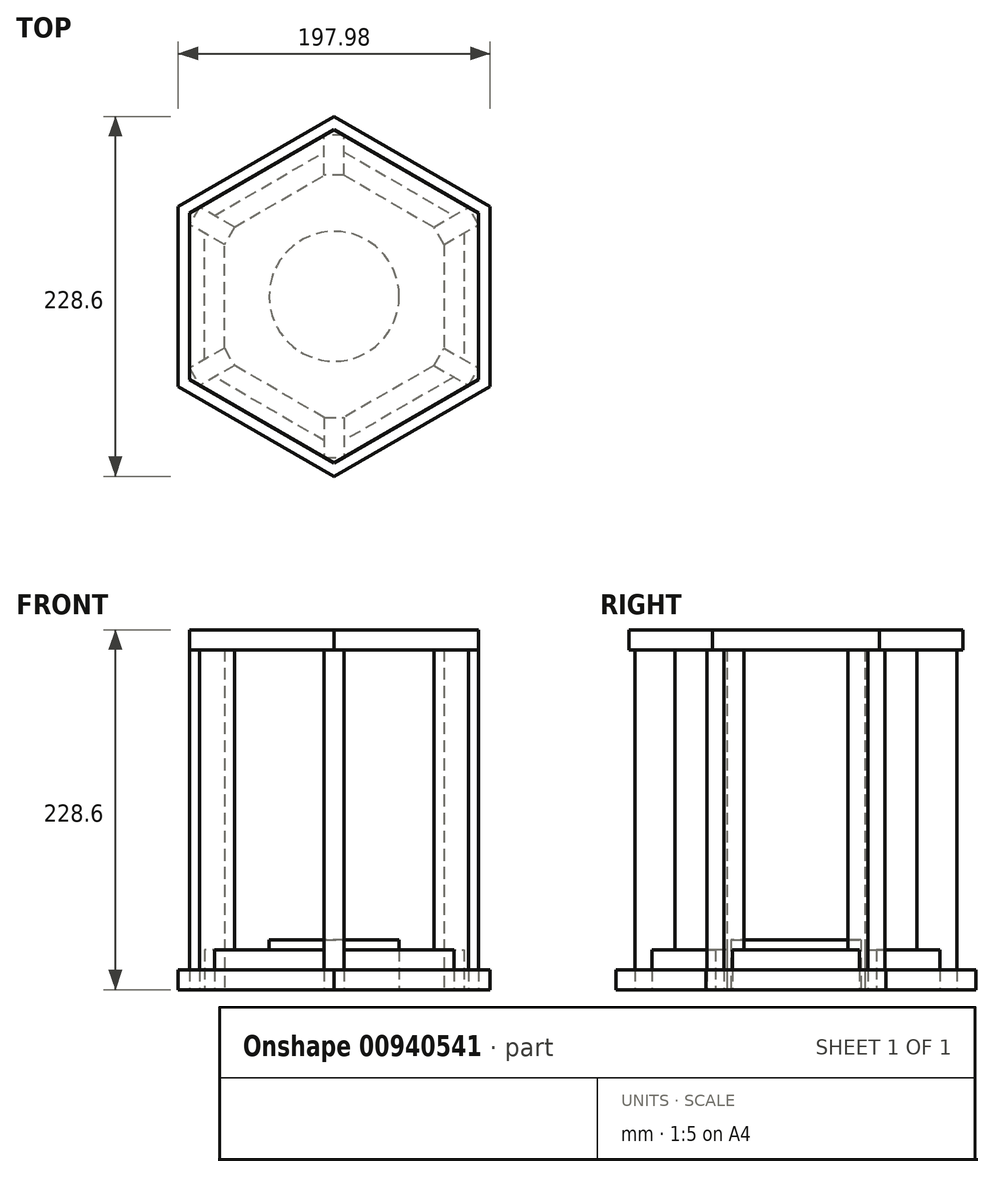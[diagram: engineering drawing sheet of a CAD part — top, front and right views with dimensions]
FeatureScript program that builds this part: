
annotation { "Feature Type Name" : "Feature", "Feature Type Description" : "" }
export const myFeature = defineFeature(function(context is Context, id is Id, definition is map)
    precondition{}
    {
        {
            var Q0;
            Q0=qCreatedBy(makeId("Top.planeOp"),FACE);
            var sketch = newSketch(context, id + "F0", { "sketchPlane" : qUnion([Q0])});
            skCircle(sketch, "E0.cCircle", {"center": v(0, 0) * mm, "radius": 82.45 * mm, "construction": true});
            skLineSegment(sketch, "E0.0", {"start": v(82.45, 47.6) * mm, "end": v(82.45, -47.6) * mm});
            skLineSegment(sketch, "E0.1", {"start": v(82.45, -47.6) * mm, "end": v(0, -95.2) * mm});
            skLineSegment(sketch, "E0.2", {"start": v(0, -95.2) * mm, "end": v(-82.45, -47.6) * mm});
            skLineSegment(sketch, "E0.3", {"start": v(-82.45, -47.6) * mm, "end": v(-82.45, 47.6) * mm});
            skLineSegment(sketch, "E0.4", {"start": v(-82.45, 47.6) * mm, "end": v(0, 95.2) * mm});
            skLineSegment(sketch, "E0.5", {"start": v(0, 95.2) * mm, "end": v(82.45, 47.6) * mm});
            skPoint(sketch, "E0.0.midPoint", {"position": v(82.45, 0) * mm});
            skCircle(sketch, "E1.cCircle", {"center": v(0, 0) * mm, "radius": 69.75 * mm, "construction": true});
            skLineSegment(sketch, "E1.0", {"start": v(69.75, 40.27) * mm, "end": v(69.75, -40.27) * mm});
            skLineSegment(sketch, "E1.1", {"start": v(69.75, -40.27) * mm, "end": v(0, -80.54) * mm});
            skLineSegment(sketch, "E1.2", {"start": v(0, -80.54) * mm, "end": v(-69.75, -40.27) * mm});
            skLineSegment(sketch, "E1.3", {"start": v(-69.75, -40.27) * mm, "end": v(-69.75, 40.27) * mm});
            skLineSegment(sketch, "E1.4", {"start": v(-69.75, 40.27) * mm, "end": v(0, 80.54) * mm});
            skLineSegment(sketch, "E1.5", {"start": v(0, 80.54) * mm, "end": v(69.75, 40.27) * mm});
            skPoint(sketch, "E1.0.midPoint", {"position": v(69.75, 0) * mm});
            skLineSegment(sketch, "E2.bottom", {"start": v(6.35, 76.88) * mm, "end": v(-6.35, 76.88) * mm});
            skLineSegment(sketch, "E2.top", {"start": v(6.35, 102.28) * mm, "end": v(-6.35, 102.28) * mm});
            skLineSegment(sketch, "E2.left", {"start": v(6.35, 76.88) * mm, "end": v(6.35, 102.28) * mm});
            skLineSegment(sketch, "E2.right", {"start": v(-6.35, 76.88) * mm, "end": v(-6.35, 102.28) * mm});
            skPoint(sketch, "E2.middle", {"position": v(0, 89.58) * mm});
            skLineSegment(sketch, "E3.1.0", {"start": v(-63.4, 43.94) * mm, "end": v(-69.75, 32.94) * mm});
            skLineSegment(sketch, "E3.1.1", {"start": v(-85.4, 56.64) * mm, "end": v(-91.75, 45.64) * mm});
            skLineSegment(sketch, "E3.1.2", {"start": v(-63.4, 43.94) * mm, "end": v(-85.4, 56.64) * mm});
            skLineSegment(sketch, "E3.1.3", {"start": v(-69.75, 32.94) * mm, "end": v(-91.75, 45.64) * mm});
            skLineSegment(sketch, "E3.2.0", {"start": v(-69.75, -32.94) * mm, "end": v(-63.4, -43.94) * mm});
            skLineSegment(sketch, "E3.2.1", {"start": v(-91.75, -45.64) * mm, "end": v(-85.4, -56.64) * mm});
            skLineSegment(sketch, "E3.2.2", {"start": v(-69.75, -32.94) * mm, "end": v(-91.75, -45.64) * mm});
            skLineSegment(sketch, "E3.2.3", {"start": v(-63.4, -43.94) * mm, "end": v(-85.4, -56.64) * mm});
            skLineSegment(sketch, "E3.3.0", {"start": v(-6.35, -76.88) * mm, "end": v(6.35, -76.88) * mm});
            skLineSegment(sketch, "E3.3.1", {"start": v(-6.35, -102.28) * mm, "end": v(6.35, -102.28) * mm});
            skLineSegment(sketch, "E3.3.2", {"start": v(-6.35, -76.88) * mm, "end": v(-6.35, -102.28) * mm});
            skLineSegment(sketch, "E3.3.3", {"start": v(6.35, -76.88) * mm, "end": v(6.35, -102.28) * mm});
            skLineSegment(sketch, "E3.4.0", {"start": v(63.4, -43.94) * mm, "end": v(69.75, -32.94) * mm});
            skLineSegment(sketch, "E3.4.1", {"start": v(85.4, -56.64) * mm, "end": v(91.75, -45.64) * mm});
            skLineSegment(sketch, "E3.4.2", {"start": v(63.4, -43.94) * mm, "end": v(85.4, -56.64) * mm});
            skLineSegment(sketch, "E3.4.3", {"start": v(69.75, -32.94) * mm, "end": v(91.75, -45.64) * mm});
            skLineSegment(sketch, "E3.5.0", {"start": v(69.75, 32.94) * mm, "end": v(63.4, 43.94) * mm});
            skLineSegment(sketch, "E3.5.1", {"start": v(91.75, 45.64) * mm, "end": v(85.4, 56.64) * mm});
            skLineSegment(sketch, "E3.5.2", {"start": v(69.75, 32.94) * mm, "end": v(91.75, 45.64) * mm});
            skLineSegment(sketch, "E3.5.3", {"start": v(63.4, 43.94) * mm, "end": v(85.4, 56.64) * mm});
            skCircle(sketch, "E4", {"center": v(0, 0) * mm, "radius": 41.28 * mm});
            skCircle(sketch, "E5.cCircle", {"center": v(0, 0) * mm, "radius": 98.99 * mm, "construction": true});
            skLineSegment(sketch, "E5.0", {"start": v(98.99, 57.15) * mm, "end": v(98.99, -57.15) * mm});
            skLineSegment(sketch, "E5.1", {"start": v(98.99, -57.15) * mm, "end": v(0, -114.3) * mm});
            skLineSegment(sketch, "E5.2", {"start": v(0, -114.3) * mm, "end": v(-98.99, -57.15) * mm});
            skLineSegment(sketch, "E5.3", {"start": v(-98.99, -57.15) * mm, "end": v(-98.99, 57.15) * mm});
            skLineSegment(sketch, "E5.4", {"start": v(-98.99, 57.15) * mm, "end": v(0, 114.3) * mm});
            skLineSegment(sketch, "E5.5", {"start": v(0, 114.3) * mm, "end": v(98.99, 57.15) * mm});
            skPoint(sketch, "E5.0.midPoint", {"position": v(98.99, 0) * mm});
            skSolve(sketch);
        }
        {
            var Q0;
            Q0=makeQuery(id+"F0.imprint","IMPRINT",FACE,{"disambiguationData":[TD([[makeQuery(id+"F0.imprint","IMPRINT",EDGE,{"derivedFrom":sQuery(id+"F0.wireOp",EDGE,"E4")}),1.0]])]});
            var Q1;
            {var subQ1=sQuery(id+"F0.wireOp",EDGE,"E3.5.1");Q1=makeQuery(id+"F0.imprint","IMPRINT",FACE,{"disambiguationData":[TD([[makeQuery(id+"F0.imprint","IMPRINT",EDGE,{"derivedFrom":subQ1}),1.0]])]});}
            var Q2;
            {var subQ0=sQuery(id+"F0.wireOp",EDGE,"E2.left");var subQ1=sQuery(id+"F0.wireOp",EDGE,"E0.5");var subQ2=makeQuery(id+"F0.imprint","INTERSECT",VERTEX,{"derivedFrom":[subQ1,subQ0]});Q2=makeQuery(id+"F0.imprint","IMPRINT",FACE,{"disambiguationData":[TD([[makeQuery(id+"F0.imprint","IMPRINT",EDGE,{"disambiguationData":[TD([[subQ2,-1.0]])],"derivedFrom":subQ1}),-1.0]])]});}
            var Q3;
            {var subQ6=sQuery(id+"F0.wireOp",EDGE,"E0.5");var subQ7=sQuery(id+"F0.wireOp",EDGE,"E0.0");var subQ8=makeQuery(id+"F0.imprint","INTERSECT",VERTEX,{"derivedFrom":[subQ7,subQ6]});Q3=makeQuery(id+"F0.imprint","IMPRINT",FACE,{"disambiguationData":[TD([[makeQuery(id+"F0.imprint","IMPRINT",EDGE,{"disambiguationData":[TD([[subQ8,-1.0]])],"derivedFrom":subQ7}),-1.0]])]});}
            var Q4;
            {var subQ1=sQuery(id+"F0.wireOp",EDGE,"E2.bottom");Q4=makeQuery(id+"F0.imprint","IMPRINT",FACE,{"disambiguationData":[TD([[makeQuery(id+"F0.imprint","IMPRINT",EDGE,{"derivedFrom":subQ1}),1.0]])]});}
            var Q5;
            {var subQ0=sQuery(id+"F0.wireOp",EDGE,"E3.4.2");var subQ1=sQuery(id+"F0.wireOp",EDGE,"E0.1");var subQ2=makeQuery(id+"F0.imprint","INTERSECT",VERTEX,{"derivedFrom":[subQ1,subQ0]});Q5=makeQuery(id+"F0.imprint","IMPRINT",FACE,{"disambiguationData":[TD([[makeQuery(id+"F0.imprint","IMPRINT",EDGE,{"disambiguationData":[TD([[subQ2,-1.0]])],"derivedFrom":subQ1}),-1.0]])]});}
            var Q6;
            {var subQ8=sQuery(id+"F0.wireOp",EDGE,"E0.2");var subQ10=sQuery(id+"F0.wireOp",EDGE,"E0.1");var subQ11=makeQuery(id+"F0.imprint","INTERSECT",VERTEX,{"derivedFrom":[subQ10,subQ8]});Q6=makeQuery(id+"F0.imprint","IMPRINT",FACE,{"disambiguationData":[TD([[makeQuery(id+"F0.imprint","IMPRINT",EDGE,{"disambiguationData":[TD([[subQ11,1.0]])],"derivedFrom":subQ10}),-1.0]])]});}
            var Q7;
            {var subQ8=sQuery(id+"F0.wireOp",EDGE,"E0.0");var subQ10=sQuery(id+"F0.wireOp",EDGE,"E0.1");var subQ11=makeQuery(id+"F0.imprint","INTERSECT",VERTEX,{"derivedFrom":[subQ8,subQ10]});Q7=makeQuery(id+"F0.imprint","IMPRINT",FACE,{"disambiguationData":[TD([[makeQuery(id+"F0.imprint","IMPRINT",EDGE,{"disambiguationData":[TD([[subQ11,1.0]])],"derivedFrom":subQ8}),-1.0]])]});}
            var Q8;
            {var subQ0=sQuery(id+"F0.wireOp",EDGE,"E3.4.1");Q8=makeQuery(id+"F0.imprint","IMPRINT",FACE,{"disambiguationData":[TD([[makeQuery(id+"F0.imprint","IMPRINT",EDGE,{"derivedFrom":subQ0}),1.0]])]});}
            var Q9;
            {var subQ31=sQuery(id+"F0.wireOp",EDGE,"E2.top");Q9=makeQuery(id+"F0.imprint","IMPRINT",FACE,{"disambiguationData":[TD([[makeQuery(id+"F0.imprint","IMPRINT",EDGE,{"derivedFrom":subQ31}),-1.0]])]});}
            var Q10;
            {var subQ0=sQuery(id+"F0.wireOp",EDGE,"E3.5.2");var subQ1=sQuery(id+"F0.wireOp",EDGE,"E0.0");var subQ2=makeQuery(id+"F0.imprint","INTERSECT",VERTEX,{"derivedFrom":[subQ1,subQ0]});Q10=makeQuery(id+"F0.imprint","IMPRINT",FACE,{"disambiguationData":[TD([[makeQuery(id+"F0.imprint","IMPRINT",EDGE,{"disambiguationData":[TD([[subQ2,-1.0]])],"derivedFrom":subQ1}),-1.0]])]});}
            var Q11;
            {var subQ1=sQuery(id+"F0.wireOp",EDGE,"E3.3.1");Q11=makeQuery(id+"F0.imprint","IMPRINT",FACE,{"disambiguationData":[TD([[makeQuery(id+"F0.imprint","IMPRINT",EDGE,{"derivedFrom":subQ1}),1.0]])]});}
            var Q12;
            {var subQ8=sQuery(id+"F0.wireOp",EDGE,"E0.5");var subQ9=sQuery(id+"F0.wireOp",EDGE,"E0.4");var subQ10=makeQuery(id+"F0.imprint","INTERSECT",VERTEX,{"derivedFrom":[subQ9,subQ8]});Q12=makeQuery(id+"F0.imprint","IMPRINT",FACE,{"disambiguationData":[TD([[makeQuery(id+"F0.imprint","IMPRINT",EDGE,{"disambiguationData":[TD([[subQ10,1.0]])],"derivedFrom":subQ9}),-1.0]])]});}
            var Q13;
            {var subQ0=sQuery(id+"F0.wireOp",EDGE,"E3.1.2");var subQ1=sQuery(id+"F0.wireOp",EDGE,"E0.4");var subQ2=makeQuery(id+"F0.imprint","INTERSECT",VERTEX,{"derivedFrom":[subQ1,subQ0]});Q13=makeQuery(id+"F0.imprint","IMPRINT",FACE,{"disambiguationData":[TD([[makeQuery(id+"F0.imprint","IMPRINT",EDGE,{"disambiguationData":[TD([[subQ2,-1.0]])],"derivedFrom":subQ1}),-1.0]])]});}
            var Q14;
            {var subQ0=sQuery(id+"F0.wireOp",EDGE,"E2.top");Q14=makeQuery(id+"F0.imprint","IMPRINT",FACE,{"disambiguationData":[TD([[makeQuery(id+"F0.imprint","IMPRINT",EDGE,{"derivedFrom":subQ0}),1.0]])]});}
            var Q15;
            {var subQ8=sQuery(id+"F0.wireOp",EDGE,"E0.4");var subQ9=sQuery(id+"F0.wireOp",EDGE,"E0.3");var subQ10=makeQuery(id+"F0.imprint","INTERSECT",VERTEX,{"derivedFrom":[subQ9,subQ8]});Q15=makeQuery(id+"F0.imprint","IMPRINT",FACE,{"disambiguationData":[TD([[makeQuery(id+"F0.imprint","IMPRINT",EDGE,{"disambiguationData":[TD([[subQ10,1.0]])],"derivedFrom":subQ9}),-1.0]])]});}
            var Q16;
            {var subQ0=sQuery(id+"F0.wireOp",EDGE,"E3.2.2");var subQ1=sQuery(id+"F0.wireOp",EDGE,"E0.3");var subQ2=makeQuery(id+"F0.imprint","INTERSECT",VERTEX,{"derivedFrom":[subQ1,subQ0]});Q16=makeQuery(id+"F0.imprint","IMPRINT",FACE,{"disambiguationData":[TD([[makeQuery(id+"F0.imprint","IMPRINT",EDGE,{"disambiguationData":[TD([[subQ2,-1.0]])],"derivedFrom":subQ1}),-1.0]])]});}
            var Q17;
            {var subQ1=sQuery(id+"F0.wireOp",EDGE,"E3.1.1");Q17=makeQuery(id+"F0.imprint","IMPRINT",FACE,{"disambiguationData":[TD([[makeQuery(id+"F0.imprint","IMPRINT",EDGE,{"derivedFrom":subQ1}),1.0]])]});}
            var Q18;
            {var subQ8=sQuery(id+"F0.wireOp",EDGE,"E0.3");var subQ9=sQuery(id+"F0.wireOp",EDGE,"E0.2");var subQ10=makeQuery(id+"F0.imprint","INTERSECT",VERTEX,{"derivedFrom":[subQ9,subQ8]});Q18=makeQuery(id+"F0.imprint","IMPRINT",FACE,{"disambiguationData":[TD([[makeQuery(id+"F0.imprint","IMPRINT",EDGE,{"disambiguationData":[TD([[subQ10,1.0]])],"derivedFrom":subQ9}),-1.0]])]});}
            var Q19;
            {var subQ0=sQuery(id+"F0.wireOp",EDGE,"E3.3.2");var subQ1=sQuery(id+"F0.wireOp",EDGE,"E0.2");var subQ2=makeQuery(id+"F0.imprint","INTERSECT",VERTEX,{"derivedFrom":[subQ1,subQ0]});Q19=makeQuery(id+"F0.imprint","IMPRINT",FACE,{"disambiguationData":[TD([[makeQuery(id+"F0.imprint","IMPRINT",EDGE,{"disambiguationData":[TD([[subQ2,-1.0]])],"derivedFrom":subQ1}),-1.0]])]});}
            var Q20;
            {var subQ1=sQuery(id+"F0.wireOp",EDGE,"E3.2.1");Q20=makeQuery(id+"F0.imprint","IMPRINT",FACE,{"disambiguationData":[TD([[makeQuery(id+"F0.imprint","IMPRINT",EDGE,{"derivedFrom":subQ1}),1.0]])]});}
            var Q21;
            {var subQ3=sQuery(id+"F0.wireOp",EDGE,"E3.3.0");Q21=makeQuery(id+"F0.imprint","IMPRINT",FACE,{"disambiguationData":[TD([[makeQuery(id+"F0.imprint","IMPRINT",EDGE,{"derivedFrom":subQ3}),-1.0]])]});}
            var Q22;
            {var subQ3=sQuery(id+"F0.wireOp",EDGE,"E2.bottom");Q22=makeQuery(id+"F0.imprint","IMPRINT",FACE,{"disambiguationData":[TD([[makeQuery(id+"F0.imprint","IMPRINT",EDGE,{"derivedFrom":subQ3}),-1.0]])]});}
            var Q23;
            {var subQ3=sQuery(id+"F0.wireOp",EDGE,"E3.4.0");Q23=makeQuery(id+"F0.imprint","IMPRINT",FACE,{"disambiguationData":[TD([[makeQuery(id+"F0.imprint","IMPRINT",EDGE,{"derivedFrom":subQ3}),-1.0]])]});}
            var Q24;
            {var subQ3=sQuery(id+"F0.wireOp",EDGE,"E3.1.0");Q24=makeQuery(id+"F0.imprint","IMPRINT",FACE,{"disambiguationData":[TD([[makeQuery(id+"F0.imprint","IMPRINT",EDGE,{"derivedFrom":subQ3}),-1.0]])]});}
            var Q25;
            {var subQ3=sQuery(id+"F0.wireOp",EDGE,"E3.2.0");Q25=makeQuery(id+"F0.imprint","IMPRINT",FACE,{"disambiguationData":[TD([[makeQuery(id+"F0.imprint","IMPRINT",EDGE,{"derivedFrom":subQ3}),-1.0]])]});}
            var Q26;
            {var subQ3=sQuery(id+"F0.wireOp",EDGE,"E3.5.0");Q26=makeQuery(id+"F0.imprint","IMPRINT",FACE,{"disambiguationData":[TD([[makeQuery(id+"F0.imprint","IMPRINT",EDGE,{"derivedFrom":subQ3}),-1.0]])]});}
            extrude(context, id + "F1", {"entities" : qUnion([Q0, Q1, Q2, Q3, Q4, Q5, Q6, Q7, Q8, Q9, Q10, Q11, Q12, Q13, Q14, Q15, Q16, Q17, Q18, Q19, Q20, Q21, Q22, Q23, Q24, Q25, Q26]), "depth" : 12.7 * mm, "offsetDistance" : 25.4 * mm});
        }
        {
            var Q0;
            {var subQ0=sQuery(id+"F0.wireOp",EDGE,"E3.2.2");var subQ1=sQuery(id+"F0.wireOp",EDGE,"E0.3");var subQ2=makeQuery(id+"F0.imprint","INTERSECT",VERTEX,{"derivedFrom":[subQ1,subQ0]});Q0=makeQuery(id+"F0.imprint","IMPRINT",FACE,{"disambiguationData":[TD([[makeQuery(id+"F0.imprint","IMPRINT",EDGE,{"disambiguationData":[TD([[subQ2,-1.0]])],"derivedFrom":subQ1}),-1.0]])]});}
            var Q1;
            {var subQ0=sQuery(id+"F0.wireOp",EDGE,"E3.1.2");var subQ1=sQuery(id+"F0.wireOp",EDGE,"E0.4");var subQ2=makeQuery(id+"F0.imprint","INTERSECT",VERTEX,{"derivedFrom":[subQ1,subQ0]});Q1=makeQuery(id+"F0.imprint","IMPRINT",FACE,{"disambiguationData":[TD([[makeQuery(id+"F0.imprint","IMPRINT",EDGE,{"disambiguationData":[TD([[subQ2,-1.0]])],"derivedFrom":subQ1}),-1.0]])]});}
            var Q2;
            {var subQ0=sQuery(id+"F0.wireOp",EDGE,"E2.left");var subQ1=sQuery(id+"F0.wireOp",EDGE,"E0.5");var subQ2=makeQuery(id+"F0.imprint","INTERSECT",VERTEX,{"derivedFrom":[subQ1,subQ0]});Q2=makeQuery(id+"F0.imprint","IMPRINT",FACE,{"disambiguationData":[TD([[makeQuery(id+"F0.imprint","IMPRINT",EDGE,{"disambiguationData":[TD([[subQ2,-1.0]])],"derivedFrom":subQ1}),-1.0]])]});}
            var Q3;
            {var subQ0=sQuery(id+"F0.wireOp",EDGE,"E3.5.2");var subQ1=sQuery(id+"F0.wireOp",EDGE,"E0.0");var subQ2=makeQuery(id+"F0.imprint","INTERSECT",VERTEX,{"derivedFrom":[subQ1,subQ0]});Q3=makeQuery(id+"F0.imprint","IMPRINT",FACE,{"disambiguationData":[TD([[makeQuery(id+"F0.imprint","IMPRINT",EDGE,{"disambiguationData":[TD([[subQ2,-1.0]])],"derivedFrom":subQ1}),-1.0]])]});}
            var Q4;
            {var subQ0=sQuery(id+"F0.wireOp",EDGE,"E3.4.2");var subQ1=sQuery(id+"F0.wireOp",EDGE,"E0.1");var subQ2=makeQuery(id+"F0.imprint","INTERSECT",VERTEX,{"derivedFrom":[subQ1,subQ0]});Q4=makeQuery(id+"F0.imprint","IMPRINT",FACE,{"disambiguationData":[TD([[makeQuery(id+"F0.imprint","IMPRINT",EDGE,{"disambiguationData":[TD([[subQ2,-1.0]])],"derivedFrom":subQ1}),-1.0]])]});}
            var Q5;
            {var subQ0=sQuery(id+"F0.wireOp",EDGE,"E3.3.2");var subQ1=sQuery(id+"F0.wireOp",EDGE,"E0.2");var subQ2=makeQuery(id+"F0.imprint","INTERSECT",VERTEX,{"derivedFrom":[subQ1,subQ0]});Q5=makeQuery(id+"F0.imprint","IMPRINT",FACE,{"disambiguationData":[TD([[makeQuery(id+"F0.imprint","IMPRINT",EDGE,{"disambiguationData":[TD([[subQ2,-1.0]])],"derivedFrom":subQ1}),-1.0]])]});}
            extrude(context, id + "F2", {"entities" : qUnion([Q0, Q1, Q2, Q3, Q4, Q5]), "depth" : 25.4 * mm, "offsetDistance" : 25.4 * mm});
        }
        {
            var Q0;
            {var subQ1=sQuery(id+"F0.wireOp",EDGE,"E3.1.1");Q0=makeQuery(id+"F0.imprint","IMPRINT",FACE,{"disambiguationData":[TD([[makeQuery(id+"F0.imprint","IMPRINT",EDGE,{"derivedFrom":subQ1}),1.0]])]});}
            var Q1;
            {var subQ8=sQuery(id+"F0.wireOp",EDGE,"E0.4");var subQ9=sQuery(id+"F0.wireOp",EDGE,"E0.3");var subQ10=makeQuery(id+"F0.imprint","INTERSECT",VERTEX,{"derivedFrom":[subQ9,subQ8]});Q1=makeQuery(id+"F0.imprint","IMPRINT",FACE,{"disambiguationData":[TD([[makeQuery(id+"F0.imprint","IMPRINT",EDGE,{"disambiguationData":[TD([[subQ10,1.0]])],"derivedFrom":subQ9}),-1.0]])]});}
            var Q2;
            {var subQ3=sQuery(id+"F0.wireOp",EDGE,"E3.1.0");Q2=makeQuery(id+"F0.imprint","IMPRINT",FACE,{"disambiguationData":[TD([[makeQuery(id+"F0.imprint","IMPRINT",EDGE,{"derivedFrom":subQ3}),-1.0]])]});}
            var Q3;
            {var subQ3=sQuery(id+"F0.wireOp",EDGE,"E3.2.0");Q3=makeQuery(id+"F0.imprint","IMPRINT",FACE,{"disambiguationData":[TD([[makeQuery(id+"F0.imprint","IMPRINT",EDGE,{"derivedFrom":subQ3}),-1.0]])]});}
            var Q4;
            {var subQ8=sQuery(id+"F0.wireOp",EDGE,"E0.3");var subQ9=sQuery(id+"F0.wireOp",EDGE,"E0.2");var subQ10=makeQuery(id+"F0.imprint","INTERSECT",VERTEX,{"derivedFrom":[subQ9,subQ8]});Q4=makeQuery(id+"F0.imprint","IMPRINT",FACE,{"disambiguationData":[TD([[makeQuery(id+"F0.imprint","IMPRINT",EDGE,{"disambiguationData":[TD([[subQ10,1.0]])],"derivedFrom":subQ9}),-1.0]])]});}
            var Q5;
            {var subQ1=sQuery(id+"F0.wireOp",EDGE,"E3.2.1");Q5=makeQuery(id+"F0.imprint","IMPRINT",FACE,{"disambiguationData":[TD([[makeQuery(id+"F0.imprint","IMPRINT",EDGE,{"derivedFrom":subQ1}),1.0]])]});}
            var Q6;
            {var subQ0=sQuery(id+"F0.wireOp",EDGE,"E2.top");Q6=makeQuery(id+"F0.imprint","IMPRINT",FACE,{"disambiguationData":[TD([[makeQuery(id+"F0.imprint","IMPRINT",EDGE,{"derivedFrom":subQ0}),1.0]])]});}
            var Q7;
            {var subQ8=sQuery(id+"F0.wireOp",EDGE,"E0.5");var subQ9=sQuery(id+"F0.wireOp",EDGE,"E0.4");var subQ10=makeQuery(id+"F0.imprint","INTERSECT",VERTEX,{"derivedFrom":[subQ9,subQ8]});Q7=makeQuery(id+"F0.imprint","IMPRINT",FACE,{"disambiguationData":[TD([[makeQuery(id+"F0.imprint","IMPRINT",EDGE,{"disambiguationData":[TD([[subQ10,1.0]])],"derivedFrom":subQ9}),-1.0]])]});}
            var Q8;
            {var subQ3=sQuery(id+"F0.wireOp",EDGE,"E2.bottom");Q8=makeQuery(id+"F0.imprint","IMPRINT",FACE,{"disambiguationData":[TD([[makeQuery(id+"F0.imprint","IMPRINT",EDGE,{"derivedFrom":subQ3}),-1.0]])]});}
            var Q9;
            {var subQ1=sQuery(id+"F0.wireOp",EDGE,"E3.5.1");Q9=makeQuery(id+"F0.imprint","IMPRINT",FACE,{"disambiguationData":[TD([[makeQuery(id+"F0.imprint","IMPRINT",EDGE,{"derivedFrom":subQ1}),1.0]])]});}
            var Q10;
            {var subQ6=sQuery(id+"F0.wireOp",EDGE,"E0.5");var subQ7=sQuery(id+"F0.wireOp",EDGE,"E0.0");var subQ8=makeQuery(id+"F0.imprint","INTERSECT",VERTEX,{"derivedFrom":[subQ7,subQ6]});Q10=makeQuery(id+"F0.imprint","IMPRINT",FACE,{"disambiguationData":[TD([[makeQuery(id+"F0.imprint","IMPRINT",EDGE,{"disambiguationData":[TD([[subQ8,-1.0]])],"derivedFrom":subQ7}),-1.0]])]});}
            var Q11;
            {var subQ3=sQuery(id+"F0.wireOp",EDGE,"E3.5.0");Q11=makeQuery(id+"F0.imprint","IMPRINT",FACE,{"disambiguationData":[TD([[makeQuery(id+"F0.imprint","IMPRINT",EDGE,{"derivedFrom":subQ3}),-1.0]])]});}
            var Q12;
            {var subQ3=sQuery(id+"F0.wireOp",EDGE,"E3.4.0");Q12=makeQuery(id+"F0.imprint","IMPRINT",FACE,{"disambiguationData":[TD([[makeQuery(id+"F0.imprint","IMPRINT",EDGE,{"derivedFrom":subQ3}),-1.0]])]});}
            var Q13;
            {var subQ8=sQuery(id+"F0.wireOp",EDGE,"E0.0");var subQ10=sQuery(id+"F0.wireOp",EDGE,"E0.1");var subQ11=makeQuery(id+"F0.imprint","INTERSECT",VERTEX,{"derivedFrom":[subQ8,subQ10]});Q13=makeQuery(id+"F0.imprint","IMPRINT",FACE,{"disambiguationData":[TD([[makeQuery(id+"F0.imprint","IMPRINT",EDGE,{"disambiguationData":[TD([[subQ11,1.0]])],"derivedFrom":subQ8}),-1.0]])]});}
            var Q14;
            {var subQ0=sQuery(id+"F0.wireOp",EDGE,"E3.4.1");Q14=makeQuery(id+"F0.imprint","IMPRINT",FACE,{"disambiguationData":[TD([[makeQuery(id+"F0.imprint","IMPRINT",EDGE,{"derivedFrom":subQ0}),1.0]])]});}
            var Q15;
            {var subQ3=sQuery(id+"F0.wireOp",EDGE,"E3.3.0");Q15=makeQuery(id+"F0.imprint","IMPRINT",FACE,{"disambiguationData":[TD([[makeQuery(id+"F0.imprint","IMPRINT",EDGE,{"derivedFrom":subQ3}),-1.0]])]});}
            var Q16;
            {var subQ8=sQuery(id+"F0.wireOp",EDGE,"E0.2");var subQ10=sQuery(id+"F0.wireOp",EDGE,"E0.1");var subQ11=makeQuery(id+"F0.imprint","INTERSECT",VERTEX,{"derivedFrom":[subQ10,subQ8]});Q16=makeQuery(id+"F0.imprint","IMPRINT",FACE,{"disambiguationData":[TD([[makeQuery(id+"F0.imprint","IMPRINT",EDGE,{"disambiguationData":[TD([[subQ11,1.0]])],"derivedFrom":subQ10}),-1.0]])]});}
            var Q17;
            {var subQ1=sQuery(id+"F0.wireOp",EDGE,"E3.3.1");Q17=makeQuery(id+"F0.imprint","IMPRINT",FACE,{"disambiguationData":[TD([[makeQuery(id+"F0.imprint","IMPRINT",EDGE,{"derivedFrom":subQ1}),1.0]])]});}
            extrude(context, id + "F3", {"entities" : qUnion([Q0, Q1, Q2, Q3, Q4, Q5, Q6, Q7, Q8, Q9, Q10, Q11, Q12, Q13, Q14, Q15, Q16, Q17]), "depth" : 215.9 * mm, "offsetDistance" : 25.4 * mm});
        }
        {
            var Q0;
            Q0=makeQuery(id+"F0.imprint","IMPRINT",FACE,{"disambiguationData":[TD([[makeQuery(id+"F0.imprint","IMPRINT",EDGE,{"derivedFrom":sQuery(id+"F0.wireOp",EDGE,"E4")}),1.0]])]});
            extrude(context, id + "F4", {"entities" : qUnion([Q0]), "depth" : 31.75 * mm, "offsetDistance" : 25.4 * mm});
        }
        {
            var Q0;
            Q0=makeQuery(id+"F3.opExtrude","CAP_FACE",FACE,{"disambiguationData":[OSD([sQuery(id+"F0.wireOp",EDGE,"E2.bottom"),sQuery(id+"F0.wireOp",EDGE,"E2.top"),sQuery(id+"F0.wireOp",EDGE,"E2.left"),sQuery(id+"F0.wireOp",EDGE,"E2.right")])],"isStart":false});
            var sketch = newSketch(context, id + "F5", { "sketchPlane" : qUnion([Q0])});
            skCircle(sketch, "E6.cCircle", {"center": v(0, 0) * mm, "radius": 91.75 * mm, "construction": true});
            skLineSegment(sketch, "E6.0", {"start": v(91.75, 52.97) * mm, "end": v(91.75, -52.97) * mm});
            skLineSegment(sketch, "E6.1", {"start": v(91.75, -52.97) * mm, "end": v(0, -105.94) * mm});
            skLineSegment(sketch, "E6.2", {"start": v(0, -105.94) * mm, "end": v(-91.75, -52.97) * mm});
            skLineSegment(sketch, "E6.3", {"start": v(-91.75, -52.97) * mm, "end": v(-91.75, 52.97) * mm});
            skLineSegment(sketch, "E6.4", {"start": v(-91.75, 52.97) * mm, "end": v(0, 105.94) * mm});
            skLineSegment(sketch, "E6.5", {"start": v(0, 105.94) * mm, "end": v(91.75, 52.97) * mm});
            skPoint(sketch, "E6.0.midPoint", {"position": v(91.75, 0) * mm});
            skSolve(sketch);
        }
        {
            var Q0;
            Q0=makeQuery(id+"F5.imprint","IMPRINT",FACE,{"disambiguationData":[TD([[makeQuery(id+"F5.imprint","IMPRINT",EDGE,{"derivedFrom":makeQuery(id+"F3.opExtrude","CAP_EDGE",EDGE,{"disambiguationData":[OSD([sQuery(id+"F0.wireOp",EDGE,"E2.bottom")])],"isStart":false})}),-1.0]])]});
            var Q1;
            {var subQ1=sQuery(id+"F5.wireOp",EDGE,"E6.0");Q1=makeQuery(id+"F5.imprint","IMPRINT",FACE,{"disambiguationData":[TD([[makeQuery(id+"F5.imprint","IMPRINT",EDGE,{"derivedFrom":subQ1}),-1.0]])]});}
            var Q2;
            {var subQ1=makeQuery(id+"F3.opExtrude","CAP_EDGE",EDGE,{"disambiguationData":[OSD([sQuery(id+"F0.wireOp",EDGE,"E2.top")])],"isStart":false});Q2=makeQuery(id+"F5.imprint","IMPRINT",FACE,{"disambiguationData":[TD([[makeQuery(id+"F5.imprint","IMPRINT",EDGE,{"derivedFrom":subQ1}),-1.0]])]});}
            extrude(context, id + "F6", {"entities" : qUnion([Q0, Q1, Q2]), "depth" : 12.7 * mm, "offsetDistance" : 25.4 * mm});
        }
    });
